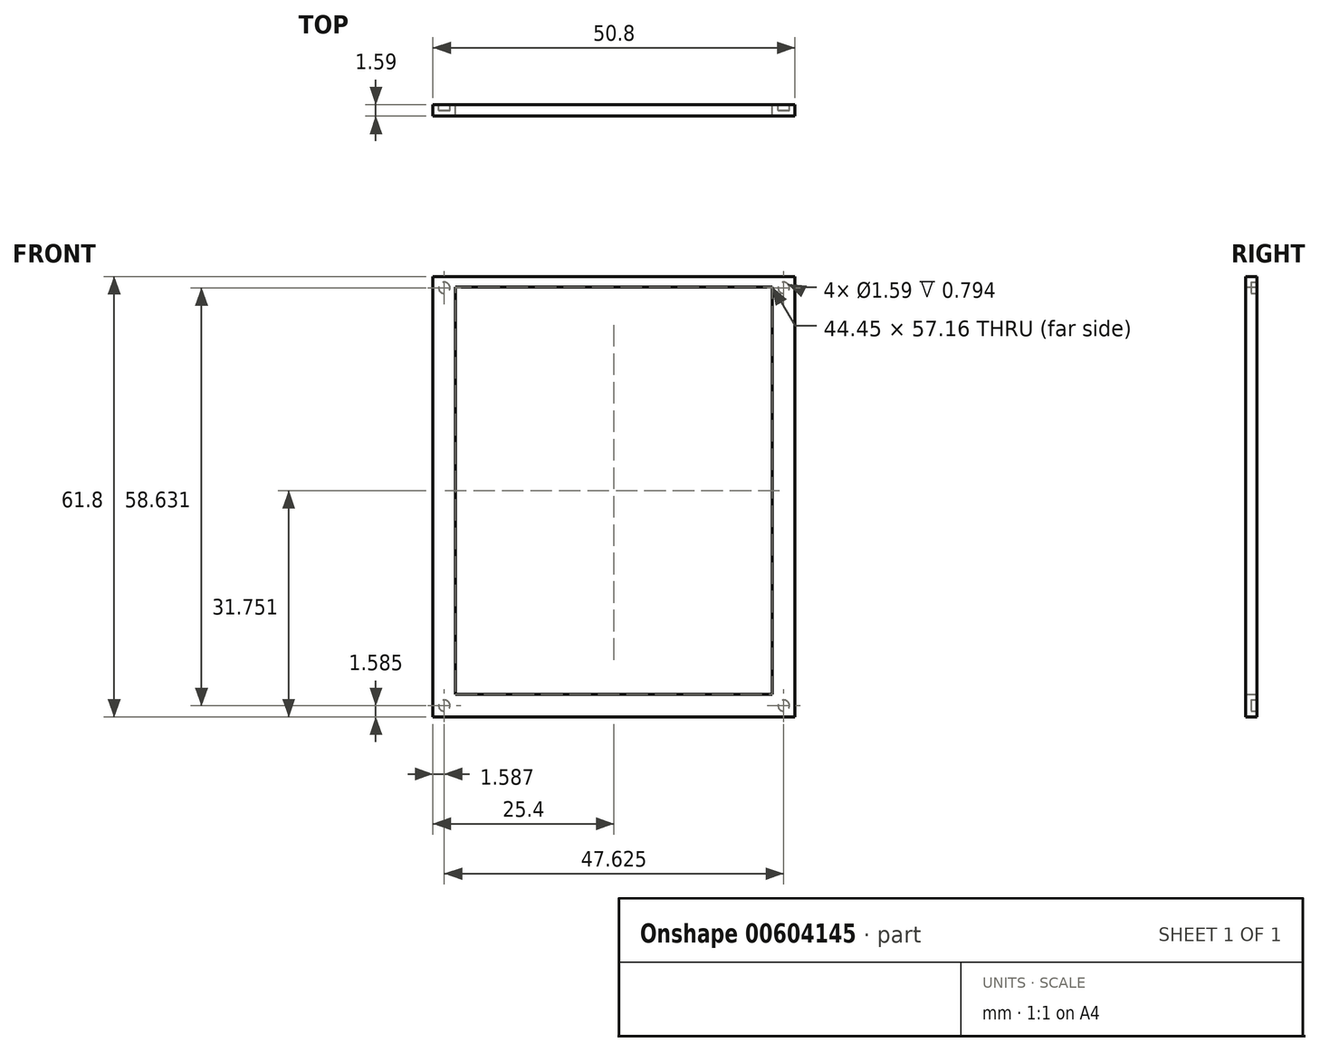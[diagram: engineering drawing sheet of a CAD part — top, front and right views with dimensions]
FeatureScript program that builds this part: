
annotation { "Feature Type Name" : "Feature", "Feature Type Description" : "" }
export const myFeature = defineFeature(function(context is Context, id is Id, definition is map)
    precondition{}
    {
        {
            var Q0;
            Q0=qCreatedBy(makeId("Front.planeOp"),FACE);
            var sketch = newSketch(context, id + "F0", { "sketchPlane" : qUnion([Q0])});
            skLineSegment(sketch, "E0.bottom", {"start": v(25.4, -30.9) * mm, "end": v(-25.4, -30.9) * mm});
            skLineSegment(sketch, "E0.top", {"start": v(25.4, 30.9) * mm, "end": v(-25.4, 30.9) * mm});
            skLineSegment(sketch, "E0.left", {"start": v(25.4, -30.9) * mm, "end": v(25.4, 30.9) * mm});
            skLineSegment(sketch, "E0.right", {"start": v(-25.4, -30.9) * mm, "end": v(-25.4, 30.9) * mm});
            skPoint(sketch, "E0.middle", {"position": v(0, 0) * mm});
            skLineSegment(sketch, "E1.bottom", {"start": v(-22.23, 29.43) * mm, "end": v(22.23, 29.43) * mm});
            skLineSegment(sketch, "E1.top", {"start": v(-22.22, -27.73) * mm, "end": v(22.23, -27.73) * mm});
            skLineSegment(sketch, "E1.left", {"start": v(-22.23, 29.43) * mm, "end": v(-22.22, -27.73) * mm});
            skLineSegment(sketch, "E1.right", {"start": v(22.22, 29.43) * mm, "end": v(22.23, -27.73) * mm});
            skSolve(sketch);
        }
        {
            var Q0;
            Q0 = qSketchRegion(id + "F0", true);
            extrude(context, id + "F1", {"entities" : qUnion([Q0]), "depth" : 1.59 * mm, "offsetDistance" : 25.4 * mm});
        }
        {
            var Q0;
            Q0=makeQuery(id+"F1.opExtrude","CAP_FACE",FACE,{"disambiguationData":[OSD([sQuery(id+"F0.wireOp",EDGE,"E0.bottom"),sQuery(id+"F0.wireOp",EDGE,"E0.top"),sQuery(id+"F0.wireOp",EDGE,"E0.left"),sQuery(id+"F0.wireOp",EDGE,"E0.right"),sQuery(id+"F0.wireOp",EDGE,"E1.bottom"),sQuery(id+"F0.wireOp",EDGE,"E1.top"),sQuery(id+"F0.wireOp",EDGE,"E1.left"),sQuery(id+"F0.wireOp",EDGE,"E1.right")])],"isStart":true});
            var sketch = newSketch(context, id + "F2", { "sketchPlane" : qUnion([Q0])});
            skCircle(sketch, "E2", {"center": v(-23.81, 29.32) * mm, "radius": 0.8 * mm});
            skCircle(sketch, "E3", {"center": v(-23.81, -29.32) * mm, "radius": 0.8 * mm});
            skCircle(sketch, "E4.MirrorC", {"center": v(23.81, -29.32) * mm, "radius": 0.8 * mm});
            skCircle(sketch, "E5.MirrorC", {"center": v(23.81, 29.32) * mm, "radius": 0.8 * mm});
            skSolve(sketch);
        }
        {
            var Q0;
            Q0 = qSketchRegion(id + "F2", true);
            extrude(context, id + "F3", {"entities" : qUnion([Q0]), "operationType" : NewBodyOperationType.REMOVE, "oppositeDirection" : true, "depth" : 0.8 * mm, "offsetDistance" : 25.4 * mm});
        }
    });
